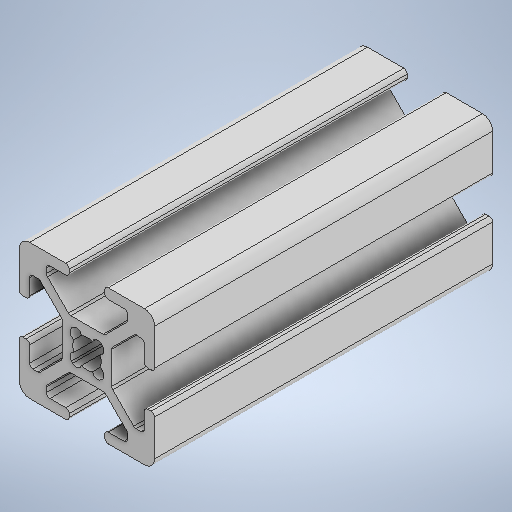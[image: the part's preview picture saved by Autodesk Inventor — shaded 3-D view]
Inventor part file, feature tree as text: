
AUTODESK INVENTOR PART (.ipt)
format: ipt  version: 2025 (Build 290162000, 162)  size: 426,496 bytes
history: native  units: mm
features: sketch x2, extrude x1, hole x1
ambient origin geometry x8: Origin, YZ Plane, XZ Plane, XY Plane, X Axis, Y Axis, Z Axis, Center Point
bodies: Solid1 (feature_tree)
feature tree (4):
  extrude  "Extrusion1"  Depth=2.384mm
  hole  "Hole2"  [1 undecoded]
  sketch  "Sketch1"  dims[d0=50.0mm d1=0.0mm]
  sketch  "Sketch3"  dims[d11=6.0mm d12=6.0mm d13=4.0mm d14=2.0mm d15=90.0deg d16=8.0mm d17=0.0mm d18=2.384mm d19=25.0mm d2=1.0mm d3=1.0mm d4=1.0mm d5=0.15mm d6=0.25mm d7=0.375mm d8=14.3117mm d9=0.75mm d10=20.594885mm]
note: 1 required parameter value undecoded (feature->parameter linkage not recoverable at this tier; creation-order binding heuristic only, values carry confidence <= 0.55)
